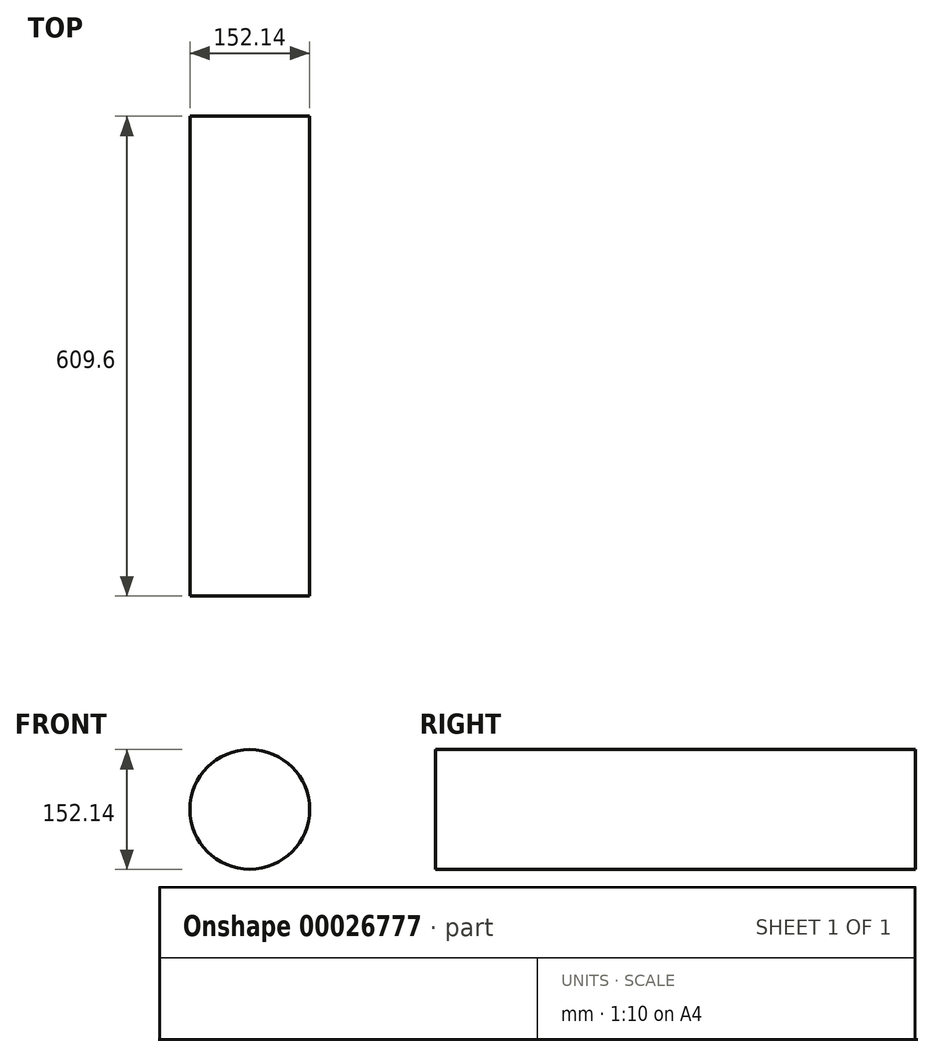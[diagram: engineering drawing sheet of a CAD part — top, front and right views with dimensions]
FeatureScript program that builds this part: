
annotation { "Feature Type Name" : "Feature", "Feature Type Description" : "" }
export const myFeature = defineFeature(function(context is Context, id is Id, definition is map)
    precondition{}
    {
        {
            var Q0;
            Q0=qCreatedBy(makeId("Front.planeOp"),FACE);
            var sketch = newSketch(context, id + "F0", { "sketchPlane" : qUnion([Q0])});
            skCircle(sketch, "E0", {"center": v(0, 0) * mm, "radius": 76.07 * mm});
            skSolve(sketch);
        }
        {
            var Q0;
            Q0=makeQuery(id+"F0.imprint","IMPRINT",FACE,{"disambiguationData":[TD([[makeQuery(id+"F0.imprint","IMPRINT",EDGE,{"derivedFrom":sQuery(id+"F0.wireOp",EDGE,"E0")}),1.0]])]});
            extrude(context, id + "F1", {"entities" : qUnion([Q0]), "depth" : 609.6 * mm});
        }
    });
